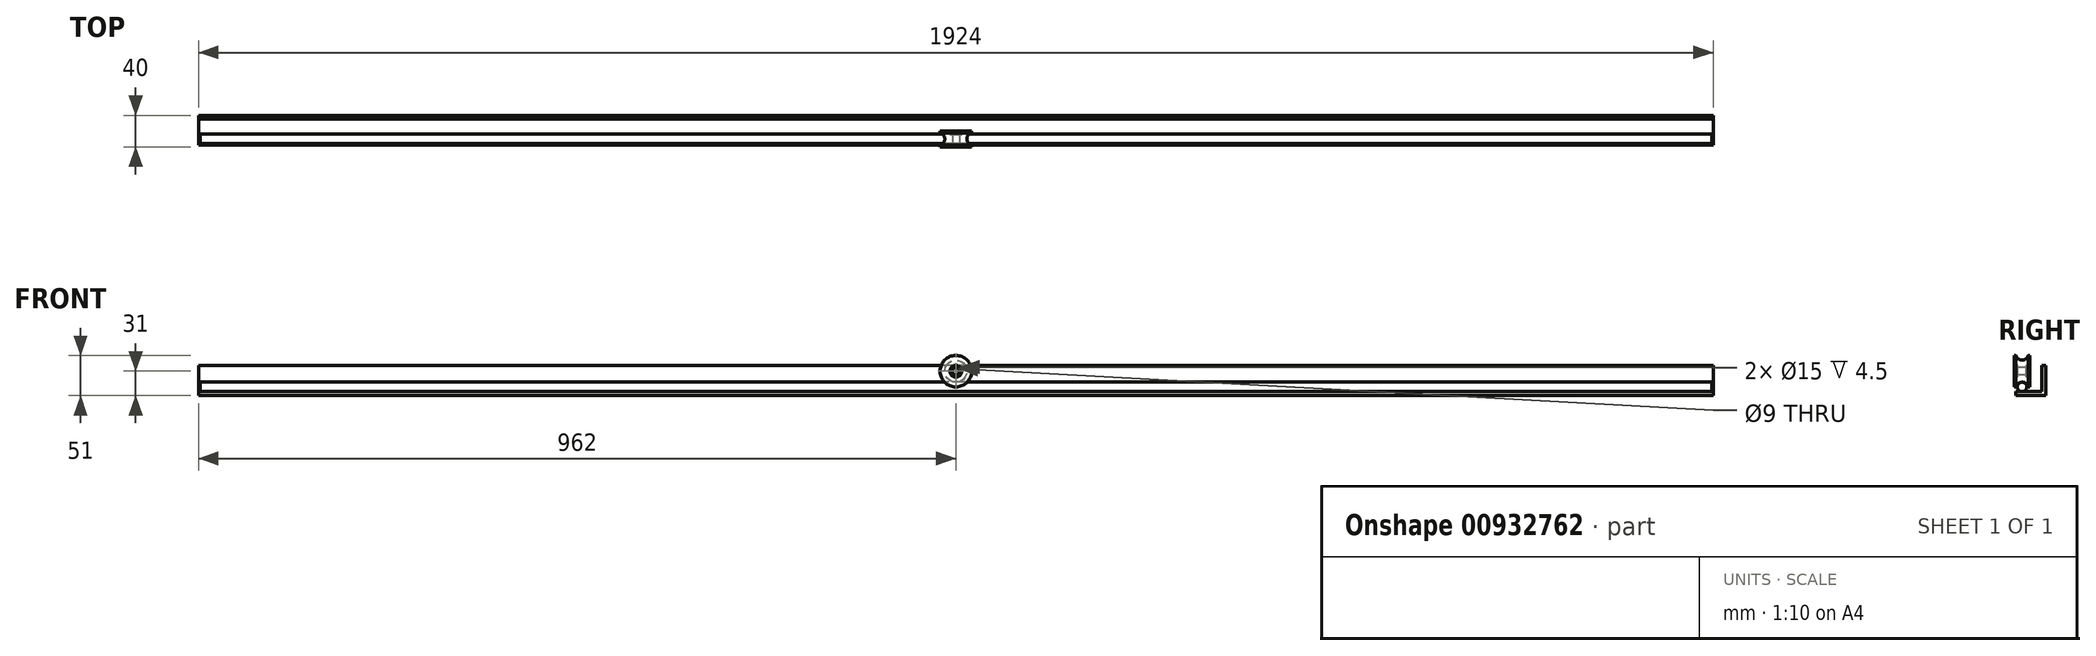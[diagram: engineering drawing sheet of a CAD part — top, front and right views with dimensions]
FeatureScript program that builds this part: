
annotation { "Feature Type Name" : "Feature", "Feature Type Description" : "" }
export const myFeature = defineFeature(function(context is Context, id is Id, definition is map)
    precondition{}
    {
        {
            var Q0;
            Q0=qCreatedBy(makeId("Right.planeOp"),FACE);
            var sketch = newSketch(context, id + "F0", { "sketchPlane" : qUnion([Q0])});
            skCircle(sketch, "E0", {"center": v(0, 0) * mm, "radius": 6 * mm});
            skSolve(sketch);
        }
        {
            var Q0;
            Q0 = qSketchRegion(id + "F0", true);
            extrude(context, id + "F1", {"entities" : qUnion([Q0]), "endBound" : BoundingType.SYMMETRIC, "depth" : 1920 * mm, "offsetDistance" : 25 * mm});
        }
        {
            var Q0;
            Q0=qCreatedBy(makeId("Right.planeOp"),FACE);
            var sketch = newSketch(context, id + "F2", { "sketchPlane" : qUnion([Q0])});
            skLineSegment(sketch, "E1.bottom", {"start": v(-5.5, 15.5) * mm, "end": v(5.5, 15.5) * mm});
            skLineSegment(sketch, "E1.top", {"start": v(-10, 0) * mm, "end": v(-7.75, 0) * mm});
            skLineSegment(sketch, "E1.left", {"start": v(-10, 12.5) * mm, "end": v(-10, 0) * mm});
            skLineSegment(sketch, "E1.right", {"start": v(10, 12.5) * mm, "end": v(10, 0) * mm});
            skLineSegment(sketch, "E2", {"start": v(-10, 12.5) * mm, "end": v(-5.5, 12.5) * mm});
            skLineSegment(sketch, "E3", {"start": v(-5.5, 12.5) * mm, "end": v(-5.5, 15.5) * mm});
            skLineSegment(sketch, "E4", {"start": v(5.5, 15.5) * mm, "end": v(5.5, 12.5) * mm});
            skLineSegment(sketch, "E5", {"start": v(5.5, 12.5) * mm, "end": v(10, 12.5) * mm});
            skLineSegment(sketch, "E6.trimOffspring", {"start": v(7.75, 0) * mm, "end": v(10, 0) * mm});
            skArc(sketch, "E7", {"start": v(7.75, 0) * mm, "mid": v(0, 6) * mm, "end": v(-7.75, 0) * mm});
            skSolve(sketch);
        }
        {
            var Q0;
            Q0=qCreatedBy(makeId("Right.planeOp"),FACE);
            var sketch = newSketch(context, id + "F3", { "sketchPlane" : qUnion([Q0])});
            skLineSegment(sketch, "E8", {"start": v(-5.66, 20) * mm, "end": v(5.64, 20) * mm});
            skSolve(sketch);
        }
        {
            var Q0;
            Q0 = qSketchRegion(id + "F2", true);
            var Q1;
            Q1=sQuery(id+"F3.wireOp",EDGE,"E8");
            revolve(context, id + "F4", {"surfaceOperationType" : NewSurfaceOperationType.NEW, "entities" : qUnion([Q0]), "axis" : qUnion([Q1]), "revolveType" : RevolveType.FULL});
        }
        {
            var Q0;
            Q0=qCreatedBy(makeId("Right.planeOp"),FACE);
            var sketch = newSketch(context, id + "F5", { "sketchPlane" : qUnion([Q0])});
            skLineSegment(sketch, "E9.bottom", {"start": v(-8, -6) * mm, "end": v(25, -6) * mm});
            skLineSegment(sketch, "E9.top", {"start": v(-8, -11) * mm, "end": v(30, -11) * mm});
            skLineSegment(sketch, "E9.left", {"start": v(-8, -6) * mm, "end": v(-8, -11) * mm});
            skLineSegment(sketch, "E10.top", {"start": v(30, 27) * mm, "end": v(25, 27) * mm});
            skLineSegment(sketch, "E10.left", {"start": v(30, -11) * mm, "end": v(30, 27) * mm});
            skLineSegment(sketch, "E10.right", {"start": v(25, -6) * mm, "end": v(25, 27) * mm});
            skSolve(sketch);
        }
        {
            var Q0;
            Q0 = qSketchRegion(id + "F5", true);
            extrude(context, id + "F6", {"entities" : qUnion([Q0]), "endBound" : BoundingType.SYMMETRIC, "depth" : 1924 * mm, "offsetDistance" : 25 * mm});
        }
    });
